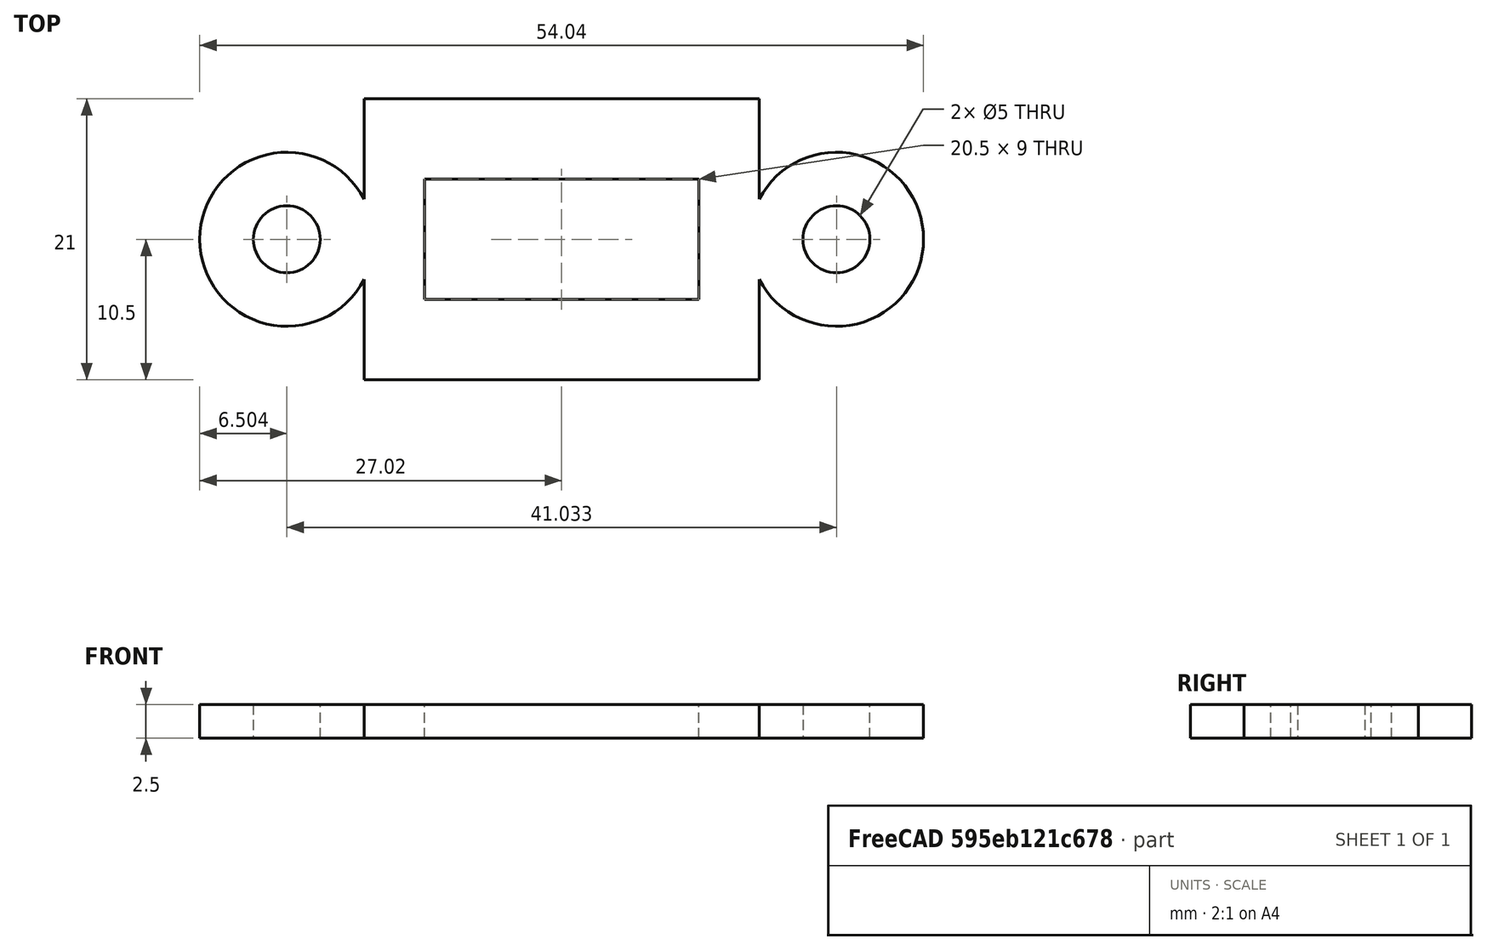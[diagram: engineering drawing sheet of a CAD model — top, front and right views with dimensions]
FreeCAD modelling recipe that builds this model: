
FCSTD DOCUMENT  (FreeCAD 0.15R4671 (Git))
Label: sensorBoard_fixTop_Connector
License: All rights reserved
LicenseURL: http://fr.wikipedia.org/wiki/<copyright redacted>
objects: Sketcher::SketchObject×1, PartDesign::Pad×1
note: 3 computed .brp shape members not serialized (recipe doc carries the construction recipe); baked Part::Feature solids carry a one-line shape summary decoded from their .brp

FEATURE [Sketcher::SketchObject] Sketch
  sketch-geometry (14):
    g0: LineSegment StartX=-10.25 StartY=4.5 StartZ=0 EndX=10.25 EndY=4.5 EndZ=0
    g1: LineSegment StartX=10.25 StartY=4.5 StartZ=0 EndX=10.25 EndY=-4.5 EndZ=0
    g2: LineSegment StartX=10.25 StartY=-4.5 StartZ=0 EndX=-10.25 EndY=-4.5 EndZ=0
    g3: LineSegment StartX=-10.25 StartY=-4.5 StartZ=0 EndX=-10.25 EndY=4.5 EndZ=0
    g4: LineSegment StartX=-14.75 StartY=10.5 StartZ=0 EndX=14.75 EndY=10.5 EndZ=0
    g5: LineSegment StartX=14.75 StartY=-10.5 StartZ=0 EndX=-14.75 EndY=-10.5 EndZ=0
    g6: Circle CenterX=-20.5163 CenterY=0 CenterZ=0 NormalX=0 NormalY=0 NormalZ=1 Radius=2.5
    g7: Circle CenterX=20.5163 CenterY=0 CenterZ=0 NormalX=0 NormalY=0 NormalZ=1 Radius=2.5
    g8: ArcOfCircle CenterX=-20.5163 CenterY=0 CenterZ=0 NormalX=0 NormalY=0 NormalZ=1 Radius=6.5 StartAngle=0.479729 EndAngle=5.80346
    g9: ArcOfCircle CenterX=20.5163 CenterY=0 CenterZ=0 NormalX=0 NormalY=0 NormalZ=1 Radius=6.5 StartAngle=3.62132 EndAngle=8.94505
    g10: LineSegment StartX=-14.75 StartY=10.5 StartZ=0 EndX=-14.75 EndY=3 EndZ=0
    g11: LineSegment StartX=-14.75 StartY=-3 StartZ=0 EndX=-14.75 EndY=-10.5 EndZ=0
    g12: LineSegment StartX=14.75 StartY=10.5 StartZ=0 EndX=14.75 EndY=3 EndZ=0
    g13: LineSegment StartX=14.75 StartY=-10.5 StartZ=0 EndX=14.75 EndY=-3 EndZ=0
  constraints (40):
    c: Coincident(g0,g1)
    c: Coincident(g1,g2)
    c: Coincident(g2,g3)
    c: Coincident(g3,g0)
    c: Horizontal(g0)
    c: Horizontal(g2)
    c: Vertical(g1)
    c: Vertical(g3)
    c: Distance(g0) = 20.5
    c: Symmetric(g2,g0,g-1)
    c: Distance(g3) = 9
    c: Horizontal(g4)
    c: Horizontal(g5)
    c: Symmetric(g5,g4,g-1)
    c: DistanceY(g0,g4) = 6
    c: Distance(g4) = 29.5
    c: Radius(g6) = 2.5
    c: Equal(g6,g7)
    c: PointOnObject(g6,g-1)
    c: PointOnObject(g7,g-1)
    c: Coincident(g8,g6)
    c: Coincident(g9,g7)
    c: Radius(g8) = 6.5
    c: Equal(g8,g9)
    c: Coincident(g10,g4)
    c: Coincident(g10,g8)
    c: Vertical(g10)
    c: Coincident(g11,g8)
    c: Coincident(g11,g5)
    c: Vertical(g11)
    c: Distance(g8,g8) = 6
    c: Vertical(g12)
    c: Coincident(g13,g5)
    c: Vertical(g13)
    c: Coincident(g9,g13)
    c: Coincident(g9,g12)
    c: Coincident(g4,g12)
    c: Equal(g4,g5)
    c: DistanceX(g9,g9) = 0
    c: Distance(g9,g9) = 6
FEATURE [PartDesign::Pad] Pad
  Length = 2.5
  Length2 = 100
  Sketch = -> Sketch
  Type = 0
